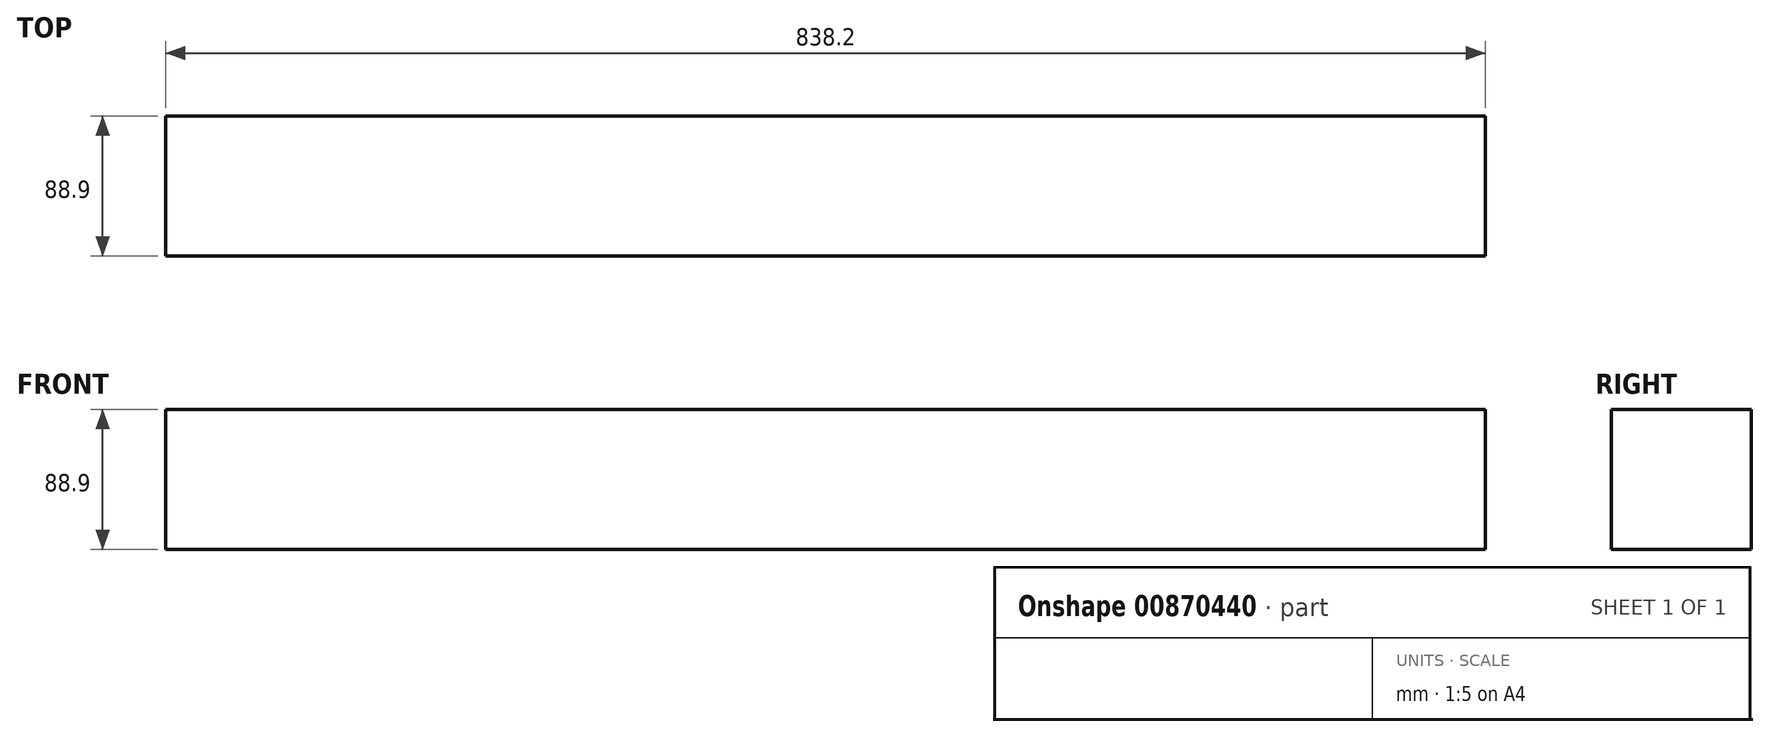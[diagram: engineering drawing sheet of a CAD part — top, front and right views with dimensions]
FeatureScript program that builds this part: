
annotation { "Feature Type Name" : "Feature", "Feature Type Description" : "" }
export const myFeature = defineFeature(function(context is Context, id is Id, definition is map)
    precondition{}
    {
        {
            var Q0;
            Q0=qCreatedBy(makeId("Right.planeOp"),FACE);
            var sketch = newSketch(context, id + "F0", { "sketchPlane" : qUnion([Q0])});
            skLineSegment(sketch, "E0.bottom", {"start": v(46.26, 44.45) * mm, "end": v(-42.64, 44.45) * mm});
            skLineSegment(sketch, "E0.top", {"start": v(46.26, -44.45) * mm, "end": v(-42.64, -44.45) * mm});
            skLineSegment(sketch, "E0.left", {"start": v(46.26, 44.45) * mm, "end": v(46.26, -44.45) * mm});
            skLineSegment(sketch, "E0.right", {"start": v(-42.64, 44.45) * mm, "end": v(-42.64, -44.45) * mm});
            skPoint(sketch, "E0.middle", {"position": v(1.8, 0) * mm});
            skSolve(sketch);
        }
        {
            var Q0;
            Q0=makeQuery(id+"F0.imprint","IMPRINT",FACE,{"disambiguationData":[TD([[makeQuery(id+"F0.imprint","IMPRINT",EDGE,{"derivedFrom":sQuery(id+"F0.wireOp",EDGE,"E0.bottom")}),1.0]])]});
            extrude(context, id + "F1", {"entities" : qUnion([Q0]), "depth" : 838.2 * mm, "offsetDistance" : 25.4 * mm});
        }
    });
